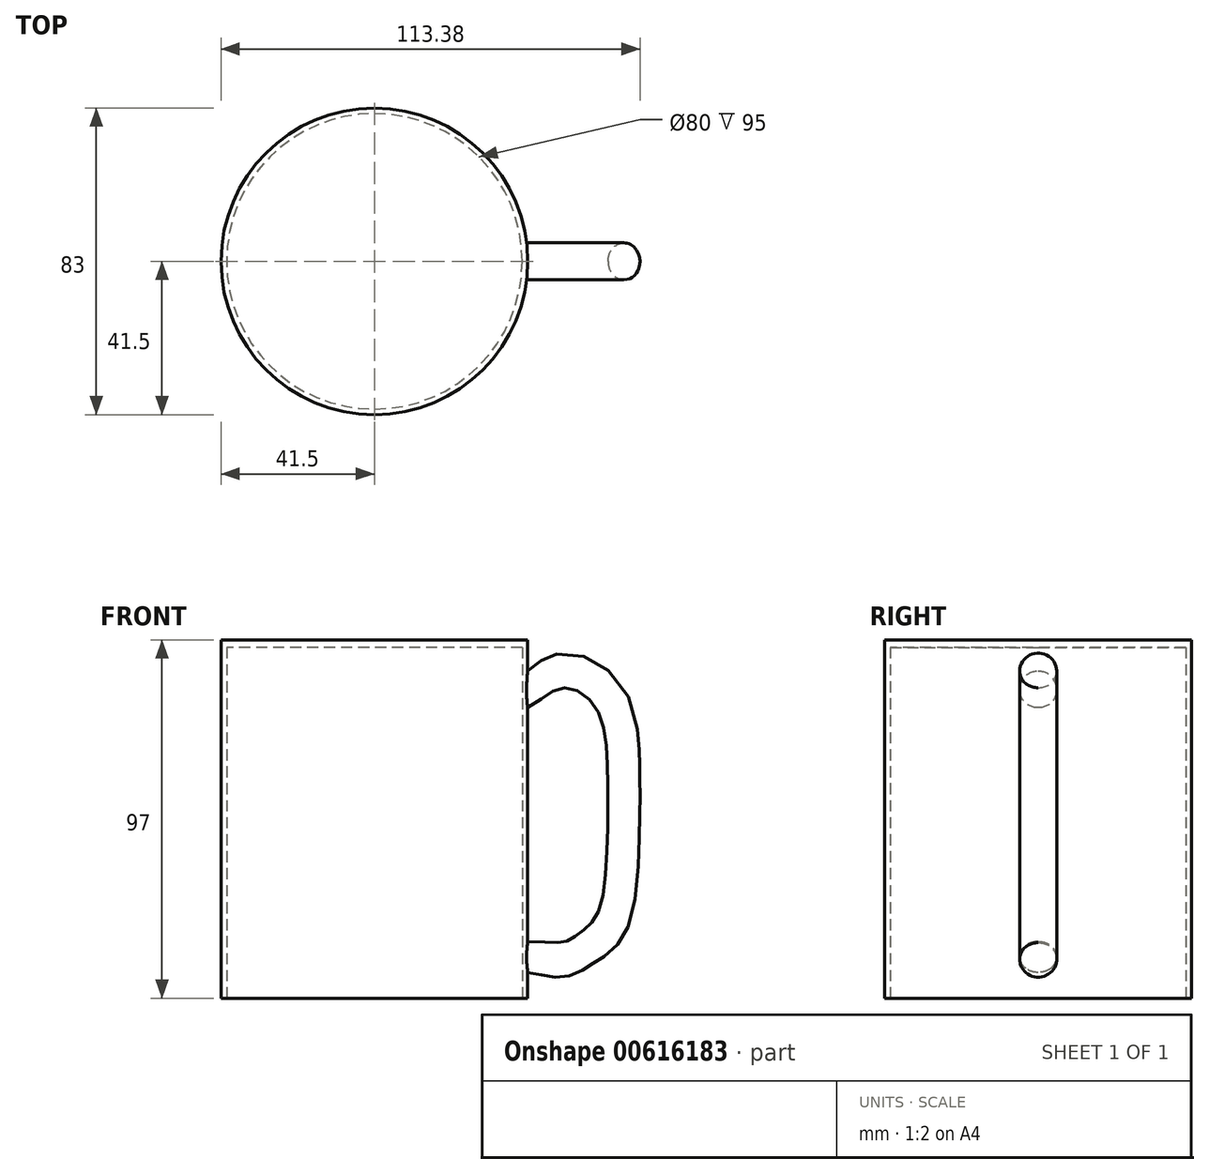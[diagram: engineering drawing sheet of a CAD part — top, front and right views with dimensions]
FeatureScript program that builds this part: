
annotation { "Feature Type Name" : "Feature", "Feature Type Description" : "" }
export const myFeature = defineFeature(function(context is Context, id is Id, definition is map)
    precondition{}
    {
        {
            var Q0;
            Q0=qCreatedBy(makeId("Top.planeOp"),FACE);
            var sketch = newSketch(context, id + "F0", { "sketchPlane" : qUnion([Q0])});
            skCircle(sketch, "E0", {"center": v(0, 0) * mm, "radius": 41.5 * mm});
            skSolve(sketch);
        }
        {
            var Q0;
            Q0 = qSketchRegion(id + "F0", true);
            extrude(context, id + "F1", {"entities" : qUnion([Q0]), "depth" : 97 * mm, "offsetDistance" : 25 * mm});
        }
        {
            var Q0;
            Q0=qCreatedBy(makeId("Front.planeOp"),FACE);
            var sketch = newSketch(context, id + "F2", { "sketchPlane" : qUnion([Q0])});
            skFitSpline(sketch, "E1", {"points": [v(35.52, 72.51) * mm, v(42.59, 80.01) * mm, v(51.26, 84.64) * mm, v(60.05, 79.6) * mm, v(63.56, 65.17) * mm, v(63.68, 43.7) * mm, v(60.97, 22.65) * mm, v(56.22, 17.44) * mm, v(51.66, 14.68) * mm, v(44.76, 14.7) * mm, v(32.55, 14.28) * mm], "startDerivative": vector(0, 123.21) * mm, "endDerivative": vector(-62.63, -9.2) * mm});
            skSolve(sketch);
        }
        {
            var Q0;
            Q0=qCreatedBy(makeId("Right.planeOp"),FACE);
            cPlane(context, id + "F3", {"entities" : qUnion([Q0]), "cplaneType" : CPlaneType.OFFSET, "offset" : 41.5 * mm, "width" : 150 * mm, "height" : 150 * mm});
        }
        {
            var Q0;
            Q0=qCreatedBy(id+"F3.planeOp",FACE);
            var sketch = newSketch(context, id + "F4", { "sketchPlane" : qUnion([Q0])});
            skCircle(sketch, "E2", {"center": v(0, 83.64) * mm, "radius": 5 * mm});
            skSolve(sketch);
        }
        {
            var Q0;
            Q0 = qSketchRegion(id + "F4", true);
            var Q1;
            Q1 = qConstructionFilter(qBodyType(qCreatedBy(id + "F2" ,EDGE), BodyType.WIRE), ConstructionObject.NO);
            sweep(context, id + "F5", {"operationType" : NewBodyOperationType.ADD, "profiles" : qUnion([Q0]), "path" : qUnion([Q1])});
        }
        {
            var Q0;
            Q0=qCreatedBy(makeId("Top.planeOp"),FACE);
            var sketch = newSketch(context, id + "F6", { "sketchPlane" : qUnion([Q0])});
            skCircle(sketch, "E3", {"center": v(0, 0) * mm, "radius": 40 * mm});
            skSolve(sketch);
        }
        {
            var Q0;
            Q0 = qSketchRegion(id + "F6", true);
            extrude(context, id + "F7", {"entities" : qUnion([Q0]), "operationType" : NewBodyOperationType.REMOVE, "depth" : 95 * mm, "offsetDistance" : 25 * mm});
        }
    });
